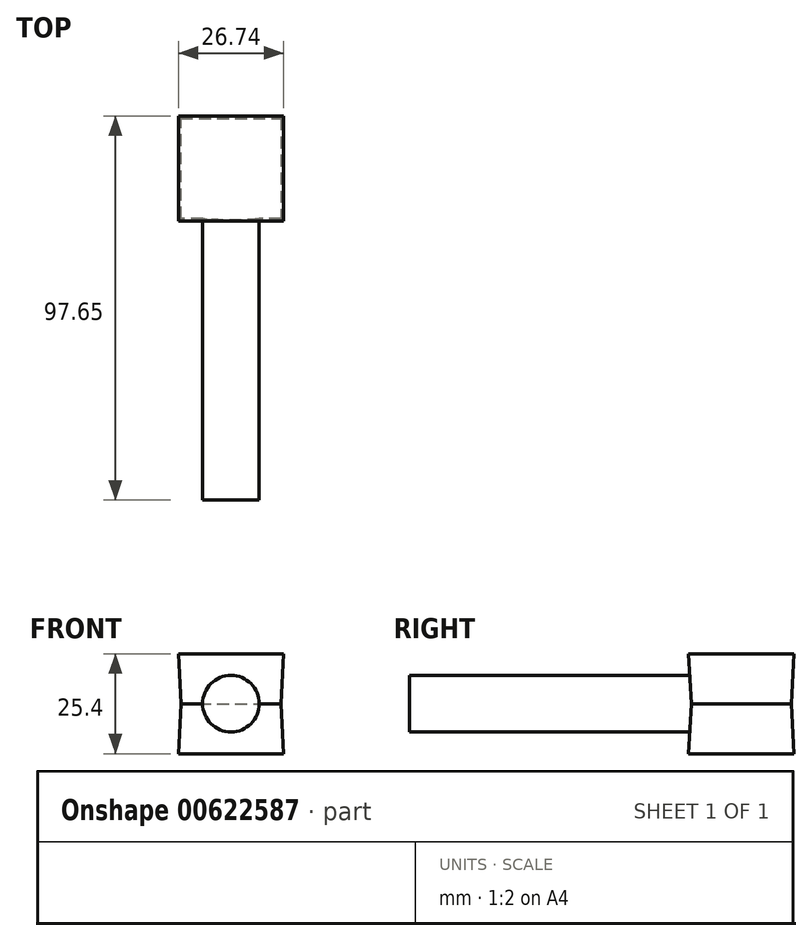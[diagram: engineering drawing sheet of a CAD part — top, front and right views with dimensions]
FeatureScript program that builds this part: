
annotation { "Feature Type Name" : "Feature", "Feature Type Description" : "" }
export const myFeature = defineFeature(function(context is Context, id is Id, definition is map)
    precondition{}
    {
        {
            var Q0;
            Q0=qCreatedBy(makeId("Top.planeOp"),FACE);
            var sketch = newSketch(context, id + "F0", { "sketchPlane" : qUnion([Q0])});
            skLineSegment(sketch, "E0", {"start": v(0, 71.58) * mm, "end": v(0, 96.98) * mm});
            skLineSegment(sketch, "E1", {"start": v(0, 96.98) * mm, "end": v(12.7, 96.98) * mm});
            skLineSegment(sketch, "E2", {"start": v(12.7, 96.98) * mm, "end": v(12.7, 71.58) * mm});
            skLineSegment(sketch, "E3", {"start": v(12.7, 71.58) * mm, "end": v(0, 71.58) * mm});
            skLineSegment(sketch, "E4.MirrorCS", {"start": v(-12.7, 96.98) * mm, "end": v(-12.7, 71.58) * mm});
            skLineSegment(sketch, "E5.MirrorCS", {"start": v(0, 96.98) * mm, "end": v(-12.7, 96.98) * mm});
            skLineSegment(sketch, "E6.MirrorCS", {"start": v(-12.7, 71.58) * mm, "end": v(0, 71.58) * mm});
            skSolve(sketch);
        }
        {
            var Q0;
            Q0=makeQuery(id+"F0.imprint","IMPRINT",FACE,{"disambiguationData":[TD([[makeQuery(id+"F0.imprint","IMPRINT",EDGE,{"derivedFrom":sQuery(id+"F0.wireOp",EDGE,"E0")}),-1.0]])]});
            var Q1;
            Q1=makeQuery(id+"F0.imprint","IMPRINT",FACE,{"disambiguationData":[TD([[makeQuery(id+"F0.imprint","IMPRINT",EDGE,{"derivedFrom":sQuery(id+"F0.wireOp",EDGE,"E0")}),1.0]])]});
            extrude(context, id + "F1", {"entities" : qUnion([Q0, Q1]), "endBound" : BoundingType.SYMMETRIC, "depth" : 25.4 * mm, "offsetDistance" : 25.4 * mm, "hasDraft" : true, "draftAngle" : 3 * degree});
        }
        {
            var Q0;
            Q0=qCreatedBy(makeId("Front.planeOp"),FACE);
            var sketch = newSketch(context, id + "F2", { "sketchPlane" : qUnion([Q0])});
            skCircle(sketch, "E7", {"center": v(0, 0) * mm, "radius": 7.19 * mm});
            skSolve(sketch);
        }
        {
            var Q0;
            Q0 = qSketchRegion(id + "F2", true);
            extrude(context, id + "F3", {"entities" : qUnion([Q0]), "operationType" : NewBodyOperationType.ADD, "endBound" : BoundingType.UP_TO_NEXT, "oppositeDirection" : true, "depth" : 25.4 * mm, "offsetDistance" : 25.4 * mm});
        }
    });
